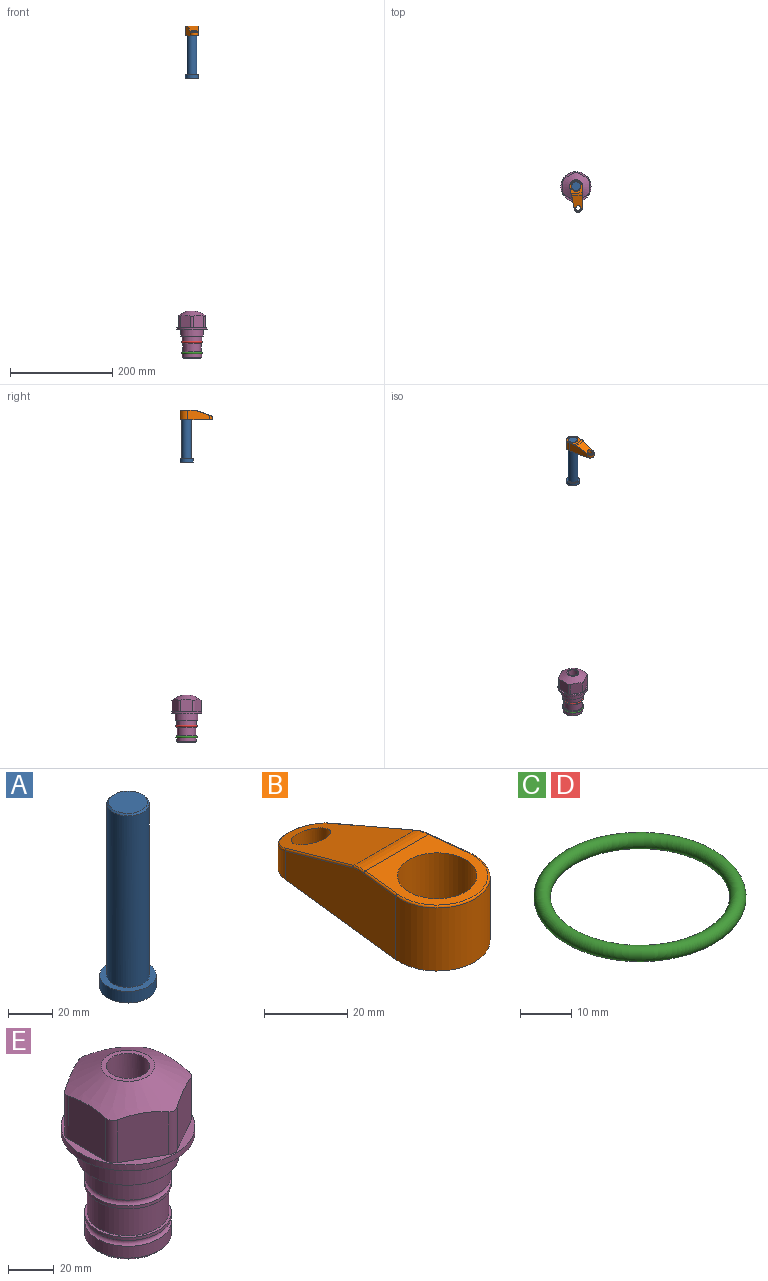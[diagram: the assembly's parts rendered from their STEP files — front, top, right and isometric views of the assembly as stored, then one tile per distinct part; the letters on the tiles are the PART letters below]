
ASSEMBLY  parts=5 mates=3
PART A: 6 faces, bbox 25.4x25.4x101.6 mm
  f0: plane 17.46x17.46mm, normal (0,0,1), area 239.5mm2, adj f5
  f1: plane 25.4x25.4mm, normal (0,0,-1), area 506.7mm2, adj f2
  f2: cylinder r=12.7mm len=25.4mm, axis (0,0,1), area 506.7mm2, adj f1,f3
  f3: plane 25.4x25.4mm, normal (0,0,1), area 221.7mm2, adj f2,f4
  f4: cylinder r=9.53mm len=94.46mm, axis (0,0,1), area 5653mm2, adj f3,f5
  f5: cone r=8.73mm half-angle=45deg, axis (0,0,-1), area 64.4mm2, adj f0,f4
PART B: 44 faces, bbox 27.5x64.5x19.1 mm
  f0: plane 2.3x0.95mm, normal (0,0,-1), area 1mm2, adj f25,f30,f34
  f1: plane 63.5x25.4mm, normal (0,0,-1), area 561.7mm2, adj f2,f3,f4,f5,f6,f7,f19,f20
  f2: cylinder r=12.7mm len=25.4mm, axis (0,0,-1), area 792.2mm2, adj f1,f3,f5,f13
  f3: plane 42.33x18.54mm, normal (0.99,0.11,0), area 647mm2, adj f1,f2,f4,f11,f12,f14
  f4: cylinder r=7.94mm len=15.78mm, axis (0,0,-1), area 158.6mm2, adj f1,f3,f5,f16
  f5: plane 42.33x18.54mm, normal (-0.99,0.11,0), area 647mm2, adj f1,f2,f4,f15,f17,f18
  f6: cylinder r=9.53mm len=19.05mm, axis (0,0,-1), area 1140.1mm2, adj f1,f8
  f7: cylinder r=4.76mm len=10.98mm, axis (0,0,-1), area 276.1mm2, adj f1,f9
  f8: plane 25.83x24.38mm, normal (0,0,1), area 262.2mm2, adj f6,f10,f11,f13,f15
  f9: plane 32.49x20.55mm, normal (0,0.34,0.94), area 489.9mm2, adj f7,f10,f14,f16,f18
  f10: cylinder r=12.7mm len=21.49mm, axis (-1,0,0), area 93.2mm2, adj f8,f9,f12,f17
  f11: cylinder r=0.51mm len=12.34mm, axis (0.11,-0.99,0), area 9.9mm2, adj f3,f8,f12,f13
  f12: bspline ~7.62x1.64mm, area 3.5mm2, adj f3,f10,f11,f14
  f13: torus R=12.19mm, axis (0,0,1), area 33.6mm2, adj f2,f8,f11,f15
  f14: cylinder r=0.51mm len=26.01mm, axis (0.1,-0.93,0.34), area 21.6mm2, adj f3,f9,f12,f16
  f15: cylinder r=0.51mm len=12.34mm, axis (0.11,0.99,0), area 9.9mm2, adj f5,f8,f13,f17
  f16: bspline ~15.78x7.05mm, area 15.7mm2, adj f4,f9,f14,f18
  f17: bspline ~7.62x1.64mm, area 3.5mm2, adj f5,f10,f15,f18
  f18: cylinder r=0.51mm len=26.01mm, axis (0.1,0.93,-0.34), area 21.6mm2, adj f5,f9,f16,f17
  f19: plane 21.6x14.29mm, normal (-0.99,-0.11,0), area 242.6mm2, adj f1,f26,f28,f34,f36,f38
  f20: plane 21.6x14.29mm, normal (0.99,-0.11,0), area 242.6mm2, adj f1,f27,f29,f37,f39,f41
  f21: cylinder r=12.7mm len=14.29mm, axis (0,0,-1), area 173.2mm2, adj f1,f26,f27,f30,f31,f33
  f22: cylinder r=7.94mm len=7.63mm, axis (0,0,-1), area 53.8mm2, adj f1,f28,f29,f42
  f23: plane 2.3x0.95mm, normal (0,0,-1), area 1mm2, adj f25,f33,f37
  f24: plane 17.94x12.32mm, normal (0,-0.34,-0.94), area 191.2mm2, adj f25,f38,f41,f42
  f25: cylinder r=9.53mm len=12.93mm, axis (-1,0,0), area 37.5mm2, adj f0,f23,f24,f31,f36,f39
  f26: cylinder r=1.59mm len=14.29mm, axis (0,0,-1), area 49mm2, adj f1,f19,f21,f32
  f27: cylinder r=1.59mm len=14.29mm, axis (0,0,-1), area 49mm2, adj f1,f20,f21,f35
  f28: cylinder r=1.59mm len=7.28mm, axis (0,0,-1), area 22.1mm2, adj f1,f19,f22,f40
  f29: cylinder r=1.59mm len=7.28mm, axis (0,0,-1), area 22.1mm2, adj f1,f20,f22,f43
  f30: torus R=14.29mm, axis (0,0,1), area 5.8mm2, adj f0,f21,f31,f32
  f31: bspline ~11.06x2.73mm, area 20.8mm2, adj f21,f25,f30,f33
  f32: sphere r=1.59mm, area 5.4mm2, adj f26,f30,f34
  f33: torus R=14.29mm, axis (0,0,1), area 5.8mm2, adj f21,f23,f31,f35
  f34: cylinder r=1.59mm len=1.68mm, axis (-0.11,0.99,0), area 2.4mm2, adj f0,f19,f32,f36
  f35: sphere r=1.59mm, area 5.4mm2, adj f27,f33,f37
  f36: bspline ~5.82x2.33mm, area 7.7mm2, adj f19,f25,f34,f38
  f37: cylinder r=1.59mm len=1.68mm, axis (0.11,0.99,0), area 2.4mm2, adj f20,f23,f35,f39
  f38: cylinder r=1.59mm len=18.33mm, axis (0.1,-0.93,0.34), area 46.7mm2, adj f19,f24,f36,f40
  f39: bspline ~5.82x2.33mm, area 7.7mm2, adj f20,f25,f37,f41
  f40: sphere r=1.59mm, area 3.6mm2, adj f28,f38,f42
  f41: cylinder r=1.59mm len=18.33mm, axis (0.1,0.93,-0.34), area 46.7mm2, adj f20,f24,f39,f43
  f42: bspline ~8.31x1.84mm, area 15.3mm2, adj f22,f24,f40,f43
  f43: sphere r=1.59mm, area 3.6mm2, adj f29,f41,f42
PART C: 1 faces, bbox 44.7x44.7x3.2 mm
  f0: torus R=19.05mm, axis (0,0,1), area 1193.9mm2
PART D: same geometry as C
PART E: 36 faces, bbox 58.7x58.7x91.2 mm
  f0: cylinder r=17.78mm len=35.56mm, axis (0,0,1), area 1670.8mm2, adj f23,f24,f31
  f1: cylinder r=19.05mm len=38.1mm, axis (0,0,1), area 1191.9mm2, adj f26,f27,f30
  f2: plane 58.66x58.66mm, normal (0,0,-1), area 1150.6mm2, adj f3,f28
  f3: cylinder r=29.33mm len=58.66mm, axis (0,0,-1), area 585.1mm2, adj f2,f4
  f4: plane 58.66x58.66mm, normal (0,0,1), area 475.9mm2, adj f3,f5,f6,f7,f8,f9,f10,f11
  f5: plane 24.5x20.32mm, normal (-0.5,0.87,0), area 562.8mm2, adj f4,f15,f16,f17
  f6: plane 24.5x20.32mm, normal (0.5,0.87,0), area 562.8mm2, adj f4,f14,f15,f17
  f7: plane 24.5x23.48mm, normal (1,0,0), area 562.8mm2, adj f4,f13,f14,f17
  f8: plane 24.5x20.32mm, normal (0.5,-0.87,0), area 562.8mm2, adj f4,f12,f13,f17
  f9: plane 24.5x20.32mm, normal (-0.5,-0.87,0), area 562.8mm2, adj f4,f11,f12,f17
  f10: plane 24.5x23.48mm, normal (-1,0,0), area 562.8mm2, adj f4,f11,f16,f17
  f11: cylinder r=5.08mm len=23.01mm, axis (0,0,-1), area 121.2mm2, adj f4,f9,f10,f17
  f12: cylinder r=5.08mm len=23.01mm, axis (0,0,-1), area 121.2mm2, adj f4,f8,f9,f17
  f13: cylinder r=5.08mm len=23.01mm, axis (0,0,-1), area 121.2mm2, adj f4,f7,f8,f17
  f14: cylinder r=5.08mm len=23.01mm, axis (0,0,-1), area 121.2mm2, adj f4,f6,f7,f17
  f15: cylinder r=5.08mm len=23.01mm, axis (0,0,-1), area 121.2mm2, adj f4,f5,f6,f17
  f16: cylinder r=5.08mm len=23.01mm, axis (0,0,-1), area 121.2mm2, adj f4,f5,f10,f17
  f17: cone r=11.73mm half-angle=60deg, axis (0,0,-1), area 2071.8mm2, adj f5,f6,f7,f8,f9,f10,f11,f12
  f18: plane 23.46x23.46mm, normal (0,0,1), area 147.4mm2, adj f17,f35
  f19: plane 34.93x34.93mm, normal (0,0,-1), area 958mm2, adj f29
  f20: cylinder r=19.05mm len=38.1mm, axis (0,0,1), area 760.1mm2, adj f21,f29
  f21: torus R=19.05mm, axis (0,0,1), area 565.3mm2, adj f20,f22
  f22: cylinder r=19.05mm len=38.1mm, axis (0,0,1), area 190mm2, adj f21,f23
  f23: plane 38.1x38.1mm, normal (0,0,1), area 146.9mm2, adj f0,f22
  f24: plane 38.1x38.1mm, normal (0,0,-1), area 146.9mm2, adj f0,f25
  f25: cylinder r=19.05mm len=38.1mm, axis (0,0,1), area 190mm2, adj f24,f26
  f26: torus R=19.05mm, axis (0,0,1), area 565.3mm2, adj f1,f25
  f27: plane 44.45x44.45mm, normal (0,0,-1), area 411.7mm2, adj f1,f28
  f28: cylinder r=22.23mm len=44.45mm, axis (0,0,1), area 1773.5mm2, adj f2,f27
  f29: cone r=19.05mm half-angle=45deg, axis (0,0,1), area 257.5mm2, adj f19,f20
  f30: cylinder r=3.17mm len=6.75mm, axis (-1,0,0), area 128mm2, adj f1,f33
  f31: cylinder r=3.17mm len=6.35mm, axis (-1,0,0), area 102.5mm2, adj f0,f33
  f32: plane 25.4x25.4mm, normal (0,0,1), area 506.7mm2, adj f33
  f33: cylinder r=12.7mm len=66.42mm, axis (0,0,-1), area 5236.2mm2, adj f30,f31,f32,f34
  f34: cone r=9.53mm half-angle=30deg, axis (0,0,-1), area 443.4mm2, adj f33,f35
  f35: cylinder r=9.53mm len=19.05mm, axis (0,0,-1), area 849mm2, adj f18,f34
PLACE A rot(axis=(0,0,-1),84.3deg) t=(0,0,518.69)mm
PLACE B rot(axis=(0,0,-1),174.3deg) t=(0,0,573.3)mm
PLACE C t=(0,0,-21.59)mm
PLACE D at identity
PLACE E at identity fixed
MATE fastened C.f0 <-> E.f0  axis (0,0,1) through (0,0,-46.1)mm
MATE cylindrical A.f2 <-> E.f0  axis (0,0,1) through (0,0,544.33)mm
MATE fastened B.f2 <-> A.f2  axis (0,0,1) through (0,0,592.35)mm
